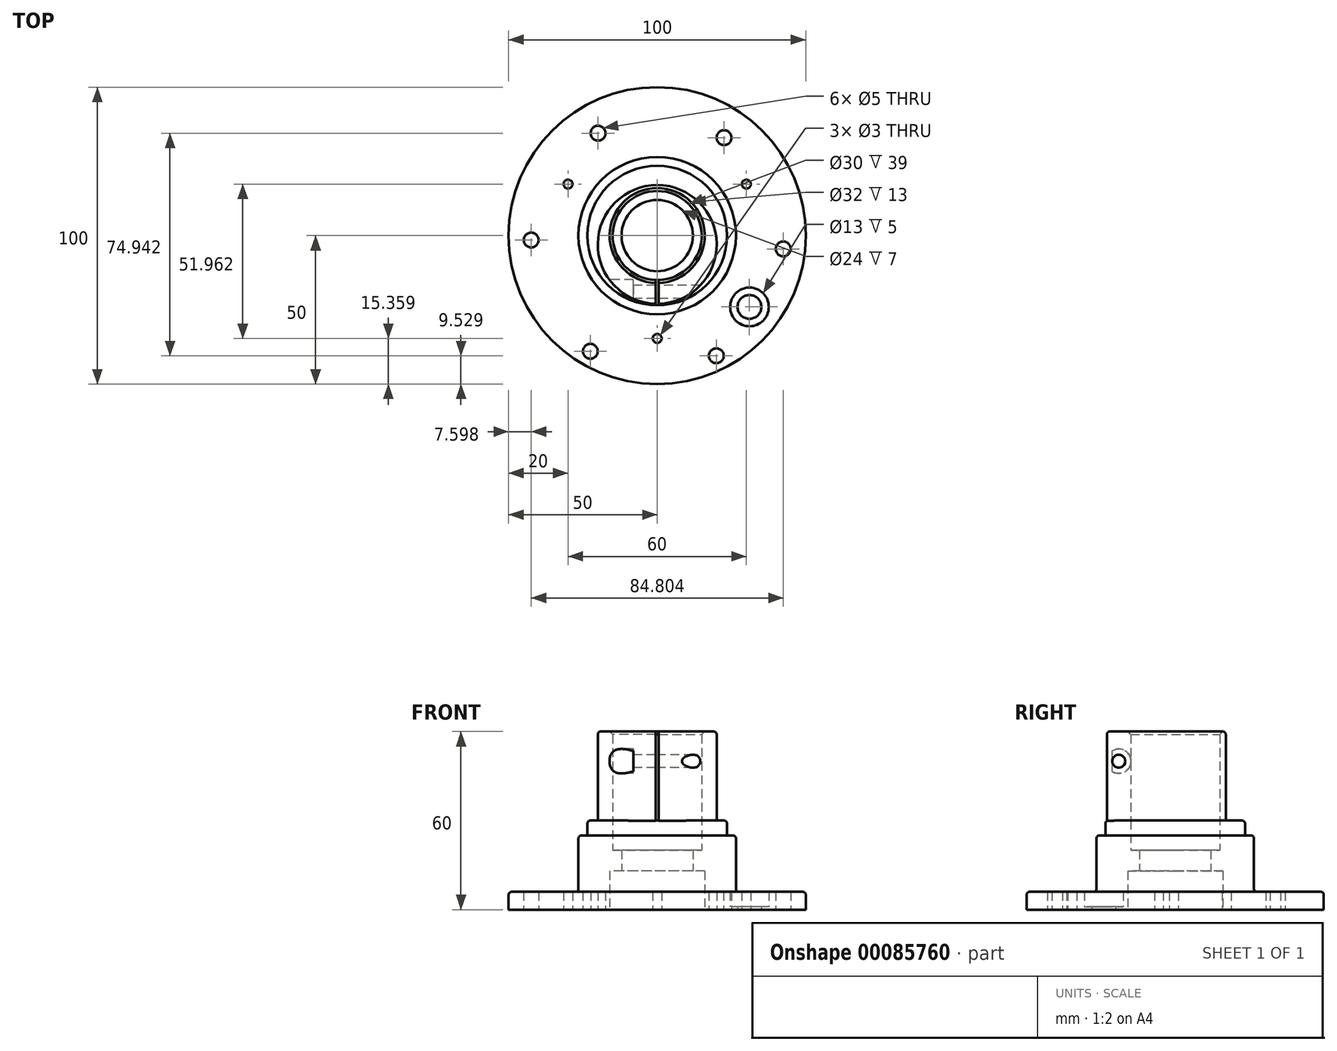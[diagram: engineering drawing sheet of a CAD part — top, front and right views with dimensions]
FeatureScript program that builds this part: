
annotation { "Feature Type Name" : "Feature", "Feature Type Description" : "" }
export const myFeature = defineFeature(function(context is Context, id is Id, definition is map)
    precondition{}
    {
        {
            var Q0;
            Q0=qCreatedBy(makeId("Top.planeOp"),FACE);
            var sketch = newSketch(context, id + "F0", { "sketchPlane" : qUnion([Q0])});
            skCircle(sketch, "E0", {"center": v(0, 0) * mm, "radius": 20 * mm});
            skSolve(sketch);
        }
        {
            var Q0;
            Q0=makeQuery(id+"F0.imprint","IMPRINT",FACE,{"disambiguationData":[TD([[makeQuery(id+"F0.imprint","IMPRINT",EDGE,{"derivedFrom":sQuery(id+"F0.wireOp",EDGE,"E0")}),1.0]])]});
            extrude(context, id + "F1", {"entities" : qUnion([Q0]), "depth" : 60 * mm});
        }
        {
            var Q0;
            Q0=qCreatedBy(makeId("Top.planeOp"),FACE);
            var sketch = newSketch(context, id + "F2", { "sketchPlane" : qUnion([Q0])});
            skCircle(sketch, "E1", {"center": v(0, 3) * mm, "radius": 23.5 * mm});
            skSolve(sketch);
        }
        {
            var Q0;
            Q0 = qSketchRegion(id + "F2", true);
            extrude(context, id + "F3", {"entities" : qUnion([Q0]), "operationType" : NewBodyOperationType.ADD, "depth" : 30 * mm});
        }
        {
            var Q0;
            Q0=qCreatedBy(makeId("Top.planeOp"),FACE);
            var sketch = newSketch(context, id + "F4", { "sketchPlane" : qUnion([Q0])});
            skCircle(sketch, "E2", {"center": v(0, 3) * mm, "radius": 15 * mm});
            skCircle(sketch, "E3", {"center": v(0, 3) * mm, "radius": 26.5 * mm});
            skSolve(sketch);
        }
        {
            var Q0;
            Q0 = qSketchRegion(id + "F4", true);
            extrude(context, id + "F5", {"entities" : qUnion([Q0]), "operationType" : NewBodyOperationType.ADD, "depth" : 25 * mm});
        }
        {
            var Q0;
            Q0=qCreatedBy(makeId("Top.planeOp"),FACE);
            var sketch = newSketch(context, id + "F6", { "sketchPlane" : qUnion([Q0])});
            skCircle(sketch, "E4", {"center": v(0, 3) * mm, "radius": 15 * mm});
            skSolve(sketch);
        }
        {
            var Q0;
            Q0 = qSketchRegion(id + "F6", true);
            extrude(context, id + "F7", {"entities" : qUnion([Q0]), "operationType" : NewBodyOperationType.REMOVE, "endBound" : BoundingType.THROUGH_ALL, "depth" : 25 * mm});
        }
        {
            var Q0;
            Q0=qCreatedBy(makeId("Top.planeOp"),FACE);
            cPlane(context, id + "F8", {"entities" : qUnion([Q0]), "cplaneType" : CPlaneType.OFFSET, "offset" : 60 * mm, "width" : 150 * mm, "height" : 150 * mm});
        }
        {
            var Q0;
            Q0=qCreatedBy(makeId("Top.planeOp"),FACE);
            var sketch = newSketch(context, id + "F9", { "sketchPlane" : qUnion([Q0])});
            skCircle(sketch, "E5", {"center": v(0, 3) * mm, "radius": 15 * mm});
            skCircle(sketch, "E6", {"center": v(0, 3) * mm, "radius": 50 * mm});
            skSolve(sketch);
        }
        {
            var Q0;
            Q0 = qSketchRegion(id + "F9", true);
            extrude(context, id + "F10", {"entities" : qUnion([Q0]), "operationType" : NewBodyOperationType.ADD, "depth" : 6 * mm});
        }
        {
            var Q0;
            Q0=qCreatedBy(id+"F8.planeOp",FACE);
            var sketch = newSketch(context, id + "F11", { "sketchPlane" : qUnion([Q0])});
            skLineSegment(sketch, "E7.bottom", {"start": v(-0.5, -10) * mm, "end": v(0.5, -10) * mm});
            skLineSegment(sketch, "E7.top", {"start": v(-0.5, -21) * mm, "end": v(0.5, -21) * mm});
            skLineSegment(sketch, "E7.left", {"start": v(-0.5, -10) * mm, "end": v(-0.5, -21) * mm});
            skLineSegment(sketch, "E7.right", {"start": v(0.5, -10) * mm, "end": v(0.5, -21) * mm});
            skSolve(sketch);
        }
        {
            var Q0;
            Q0 = qSketchRegion(id + "F11", true);
            extrude(context, id + "F12", {"entities" : qUnion([Q0]), "operationType" : NewBodyOperationType.REMOVE, "oppositeDirection" : true, "depth" : 30 * mm});
        }
        {
            var Q0;
            Q0=qCreatedBy(makeId("Right.planeOp"),FACE);
            cPlane(context, id + "F13", {"entities" : qUnion([Q0]), "cplaneType" : CPlaneType.OFFSET, "offset" : 16 * mm, "oppositeDirection" : true, "width" : 150 * mm, "height" : 150 * mm});
        }
        {
            var Q0;
            Q0=qCreatedBy(id+"F13.planeOp",FACE);
            var sketch = newSketch(context, id + "F14", { "sketchPlane" : qUnion([Q0])});
            skPoint(sketch, "E8.center.orphan", {"position": v(-16, 50) * mm});
            skSolve(sketch);
        }
        {
            var Q0;
            Q0=sQuery(id+"F14.wireOp",VERTEX,"E8.center.orphan");
            var Q1;
            Q1=makeQuery(id+"F1.opExtrude","SWEPT_BODY",BODY,{"disambiguationData":[OSD([sQuery(id+"F0.wireOp",EDGE,"E0")])]});
            hole(context, id + "F15", {"style" : HoleStyle.C_BORE, "endStyle" : HoleEndStyle.BLIND, "oppositeDirection" : true, "holeDiameter" : 4.4 * mm, "cBoreDiameter" : 8.25 * mm, "cBoreDepth" : 8 * mm, "holeDepth" : 40 * mm, "locations" : qUnion([Q0]), "scope" : qUnion([Q1])});
        }
        {
            var Q0;
            Q0=qCreatedBy(makeId("Top.planeOp"),FACE);
            var sketch = newSketch(context, id + "F16", { "sketchPlane" : qUnion([Q0])});
            skCircle(sketch, "E9", {"center": v(0, 3) * mm, "radius": 15 * mm});
            skCircle(sketch, "E10", {"center": v(0, 3) * mm, "radius": 16 * mm});
            skSolve(sketch);
        }
        {
            var Q0;
            Q0 = qSketchRegion(id + "F16", true);
            extrude(context, id + "F17", {"entities" : qUnion([Q0]), "operationType" : NewBodyOperationType.REMOVE, "depth" : 13 * mm});
        }
        {
            var Q0;
            Q0=qCreatedBy(makeId("Top.planeOp"),FACE);
            var sketch = newSketch(context, id + "F18", { "sketchPlane" : qUnion([Q0])});
            skCircle(sketch, "E11", {"center": v(0, 3) * mm, "radius": 7.3 * mm, "construction": true});
            skCircle(sketch, "E12.cCircle", {"center": v(0, 3) * mm, "radius": 17.32 * mm, "construction": true});
            skLineSegment(sketch, "E12.0", {"start": v(30, 20.32) * mm, "end": v(0, -31.64) * mm, "construction": true});
            skLineSegment(sketch, "E12.1", {"start": v(0, -31.64) * mm, "end": v(-30, 20.32) * mm, "construction": true});
            skLineSegment(sketch, "E12.2", {"start": v(-30, 20.32) * mm, "end": v(30, 20.32) * mm, "construction": true});
            skPoint(sketch, "E12.0.midPoint", {"position": v(15, -5.66) * mm});
            skLineSegment(sketch, "E13", {"start": v(0, -31.64) * mm, "end": v(0, 0) * mm, "construction": true});
            skCircle(sketch, "E14", {"center": v(-30, 20.32) * mm, "radius": 1.5 * mm});
            skCircle(sketch, "E15", {"center": v(30, 20.32) * mm, "radius": 1.5 * mm});
            skCircle(sketch, "E16", {"center": v(0, -31.64) * mm, "radius": 1.5 * mm});
            skSolve(sketch);
        }
        {
            var Q0;
            Q0 = qSketchRegion(id + "F18", true);
            extrude(context, id + "F19", {"entities" : qUnion([Q0]), "operationType" : NewBodyOperationType.REMOVE, "depth" : 25 * mm});
        }
        {
            var Q0;
            Q0=qCreatedBy(makeId("Top.planeOp"),FACE);
            var sketch = newSketch(context, id + "F20", { "sketchPlane" : qUnion([Q0])});
            skCircle(sketch, "E17", {"center": v(0, 3) * mm, "radius": 7.87 * mm, "construction": true});
            skCircle(sketch, "E18.cCircle", {"center": v(0, 3) * mm, "radius": 45 * mm, "construction": true});
            skLineSegment(sketch, "E18.0", {"start": v(22.5, -35.97) * mm, "end": v(-22.5, -35.97) * mm, "construction": true});
            skLineSegment(sketch, "E18.1", {"start": v(-22.5, -35.97) * mm, "end": v(-45, 3) * mm, "construction": true});
            skLineSegment(sketch, "E18.2", {"start": v(-45, 3) * mm, "end": v(-22.5, 41.97) * mm, "construction": true});
            skLineSegment(sketch, "E18.3", {"start": v(-22.5, 41.97) * mm, "end": v(22.5, 41.97) * mm, "construction": true});
            skLineSegment(sketch, "E18.4", {"start": v(22.5, 41.97) * mm, "end": v(45, 3) * mm, "construction": true});
            skLineSegment(sketch, "E18.5", {"start": v(45, 3) * mm, "end": v(22.5, -35.97) * mm, "construction": true});
            skCircle(sketch, "E19", {"center": v(-22.5, -35.97) * mm, "radius": 2.5 * mm});
            skCircle(sketch, "E20.1.0", {"center": v(19.9, -37.47) * mm, "radius": 2.5 * mm});
            skCircle(sketch, "E20.2.0", {"center": v(42.4, -1.5) * mm, "radius": 2.5 * mm});
            skCircle(sketch, "E20.3.0", {"center": v(22.5, 35.97) * mm, "radius": 2.5 * mm});
            skCircle(sketch, "E20.4.0", {"center": v(-19.9, 37.47) * mm, "radius": 2.5 * mm});
            skCircle(sketch, "E20.5.0", {"center": v(-42.4, 1.5) * mm, "radius": 2.5 * mm});
            skPoint(sketch, "E20.center", {"position": v(0, 0) * mm});
            skSolve(sketch);
        }
        {
            var Q0;
            Q0 = qSketchRegion(id + "F20", true);
            extrude(context, id + "F21", {"entities" : qUnion([Q0]), "operationType" : NewBodyOperationType.REMOVE, "depth" : 25 * mm});
        }
        {
            var Q0;
            Q0=qCreatedBy(makeId("Top.planeOp"),FACE);
            var sketch = newSketch(context, id + "F22", { "sketchPlane" : qUnion([Q0])});
            skCircle(sketch, "E21", {"center": v(0, 0) * mm, "radius": 37.5 * mm, "construction": true});
            skCircle(sketch, "E22", {"center": v(31.05, -21.03) * mm, "radius": 4 * mm});
            skCircle(sketch, "E23", {"center": v(-30, 20.32) * mm, "radius": 7 * mm, "construction": true});
            skLineSegment(sketch, "E24", {"start": v(-30, 20.32) * mm, "end": v(53.18, -36.02) * mm, "construction": true});
            skSolve(sketch);
        }
        {
            var Q0;
            Q0 = qSketchRegion(id + "F22", true);
            extrude(context, id + "F23", {"entities" : qUnion([Q0]), "operationType" : NewBodyOperationType.REMOVE, "depth" : 25 * mm});
        }
        {
            var Q0;
            Q0=qCreatedBy(makeId("Top.planeOp"),FACE);
            cPlane(context, id + "F24", {"entities" : qUnion([Q0]), "cplaneType" : CPlaneType.OFFSET, "offset" : 1 * mm, "width" : 150 * mm, "height" : 150 * mm});
        }
        {
            var Q0;
            Q0=qCreatedBy(id+"F24.planeOp",FACE);
            var sketch = newSketch(context, id + "F25", { "sketchPlane" : qUnion([Q0])});
            skCircle(sketch, "E25", {"center": v(31.05, -21.03) * mm, "radius": 4 * mm});
            skCircle(sketch, "E26", {"center": v(31.05, -21.03) * mm, "radius": 6.5 * mm});
            skSolve(sketch);
        }
        {
            var Q0;
            Q0 = qSketchRegion(id + "F25", true);
            extrude(context, id + "F26", {"entities" : qUnion([Q0]), "operationType" : NewBodyOperationType.REMOVE, "depth" : 10 * mm});
        }
        {
            var Q0;
            Q0=makeQuery(id+"F1.opExtrude","CAP_EDGE",EDGE,{"disambiguationData":[OSD([sQuery(id+"F0.wireOp",EDGE,"E0")])],"isStart":false});
            var Q1;
            Q1=makeQuery(id+"F5.opExtrude","CAP_EDGE",EDGE,{"disambiguationData":[OSD([sQuery(id+"F4.wireOp",EDGE,"E3")])],"isStart":false});
            var Q2;
            Q2=makeQuery(id+"F3.opExtrude","CAP_EDGE",EDGE,{"disambiguationData":[OSD([sQuery(id+"F2.wireOp",EDGE,"E1")])],"isStart":false});
            var Q3;
            Q3=makeQuery(id+"F10.opExtrude","CAP_EDGE",EDGE,{"disambiguationData":[OSD([sQuery(id+"F9.wireOp",EDGE,"E6")])],"isStart":false});
            var Q4;
            Q4=makeQuery(id+"F10.boolean.opBoolean","INTERSECT",EDGE,{"derivedFrom":[makeQuery(id+"F5.opExtrude","SWEPT_FACE",FACE,{"disambiguationData":[OSD([sQuery(id+"F4.wireOp",EDGE,"E3")])]}),makeQuery(id+"F10.opExtrude","CAP_FACE",FACE,{"disambiguationData":[OSD([sQuery(id+"F9.wireOp",EDGE,"E5"),sQuery(id+"F9.wireOp",EDGE,"E6")])],"isStart":false})]});
            fillet(context, id + "F27", {"entities" : qUnion([Q0, Q1, Q2, Q3, Q4]), "radius" : 1 * mm, "tangentPropagation" : true, "allowEdgeOverflow" : false});
        }
        {
            var Q0;
            Q0=makeQuery(id+"F7.boolean.opBoolean","INTERSECT",EDGE,{"derivedFrom":[makeQuery(id+"F1.opExtrude","CAP_FACE",FACE,{"disambiguationData":[OSD([sQuery(id+"F0.wireOp",EDGE,"E0")])],"isStart":false}),makeQuery(id+"F7.opExtrude","SWEPT_FACE",FACE,{"disambiguationData":[OSD([sQuery(id+"F6.wireOp",EDGE,"E4")])]})]});
            chamfer(context, id + "F28", {"entities" : qUnion([Q0]), "width" : 1 * mm, "tangentPropagation" : true});
        }
        {
            var Q0;
            Q0=qCreatedBy(makeId("Top.planeOp"),FACE);
            cPlane(context, id + "F29", {"entities" : qUnion([Q0]), "cplaneType" : CPlaneType.OFFSET, "offset" : 13 * mm, "width" : 150 * mm, "height" : 150 * mm});
        }
        {
            var Q0;
            Q0=qCreatedBy(id+"F29.planeOp",FACE);
            var sketch = newSketch(context, id + "F30", { "sketchPlane" : qUnion([Q0])});
            skCircle(sketch, "E27", {"center": v(0, 3) * mm, "radius": 18 * mm});
            skCircle(sketch, "E28", {"center": v(0, 3) * mm, "radius": 12 * mm});
            skSolve(sketch);
        }
        {
            var Q0;
            Q0 = qSketchRegion(id + "F30", true);
            extrude(context, id + "F31", {"entities" : qUnion([Q0]), "operationType" : NewBodyOperationType.ADD, "depth" : 7 * mm});
        }
    });
